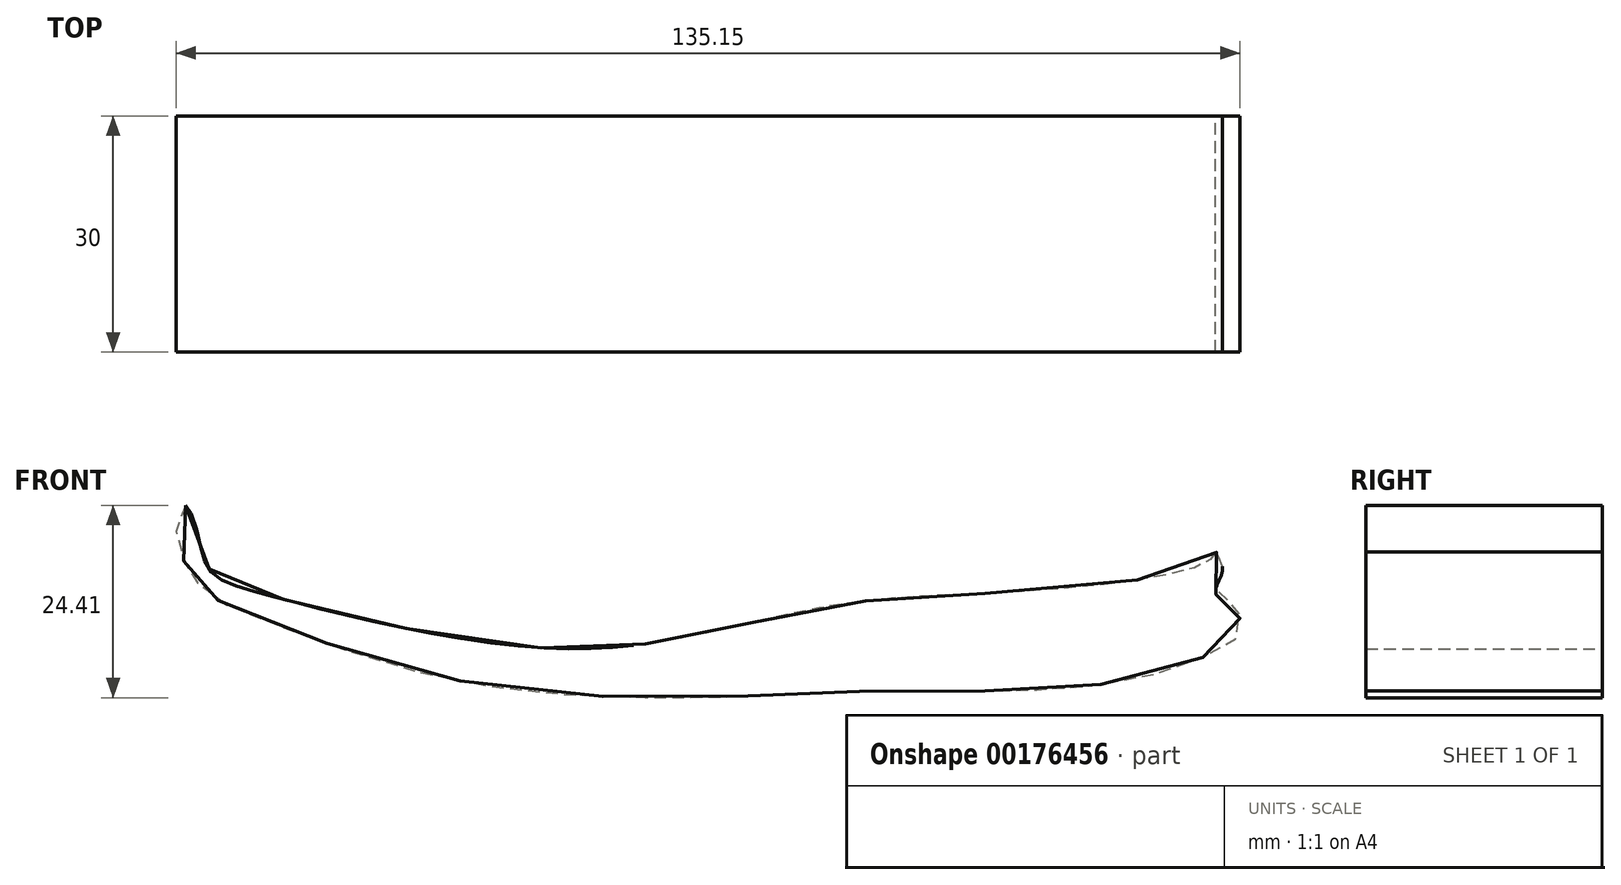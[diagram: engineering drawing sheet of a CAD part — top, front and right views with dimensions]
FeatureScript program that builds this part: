
annotation { "Feature Type Name" : "Feature", "Feature Type Description" : "" }
export const myFeature = defineFeature(function(context is Context, id is Id, definition is map)
    precondition{}
    {
        {
            var Q0;
            Q0=qCreatedBy(makeId("Front.planeOp"),FACE);
            var sketch = newSketch(context, id + "F0", { "sketchPlane" : qUnion([Q0])});
            skFitSpline(sketch, "E0", {"points": [v(-69, -3.45) * mm, v(-70.08, -5.35) * mm, v(-69.4, -10.19) * mm, v(-68.1, -11.89) * mm, v(-66.95, -14) * mm, v(-59.25, -17.88) * mm, v(-41.28, -24.08) * mm, v(-21.13, -27.41) * mm, v(1.75, -27.68) * mm, v(14.9, -27.07) * mm, v(31.17, -27) * mm, v(45.6, -26.4) * mm, v(57.72, -23.74) * mm, v(64.05, -20.67) * mm, v(64.87, -19.45) * mm, v(64.66, -16.52) * mm, v(63.98, -16.1) * mm, v(63.3, -15.43) * mm, v(61.87, -14.68) * mm, v(62.69, -11.96) * mm, v(62.42, -10.32) * mm, v(61.94, -9.37) * mm, v(61.26, -10.25) * mm, v(45.2, -13.73) * mm, v(24.08, -15.02) * mm, v(11.9, -16.38) * mm, v(-2.67, -19.58) * mm, v(-13.57, -21.35) * mm, v(-26.16, -21.35) * mm, v(-46.11, -17.95) * mm, v(-59.73, -14.48) * mm, v(-65.52, -12.1) * mm, v(-67.22, -8) * mm, v(-69, -3.45) * mm]});
            skSolve(sketch);
        }
        {
            var Q0;
            Q0=makeQuery(id+"F0.imprint","IMPRINT",FACE,{"disambiguationData":[TD([[makeQuery(id+"F0.imprint","IMPRINT",EDGE,{"derivedFrom":sQuery(id+"F0.wireOp",EDGE,"E0")}),1.0]])]});
            extrude(context, id + "F1", {"entities" : qUnion([Q0]), "depth" : 30 * mm});
        }
    });
